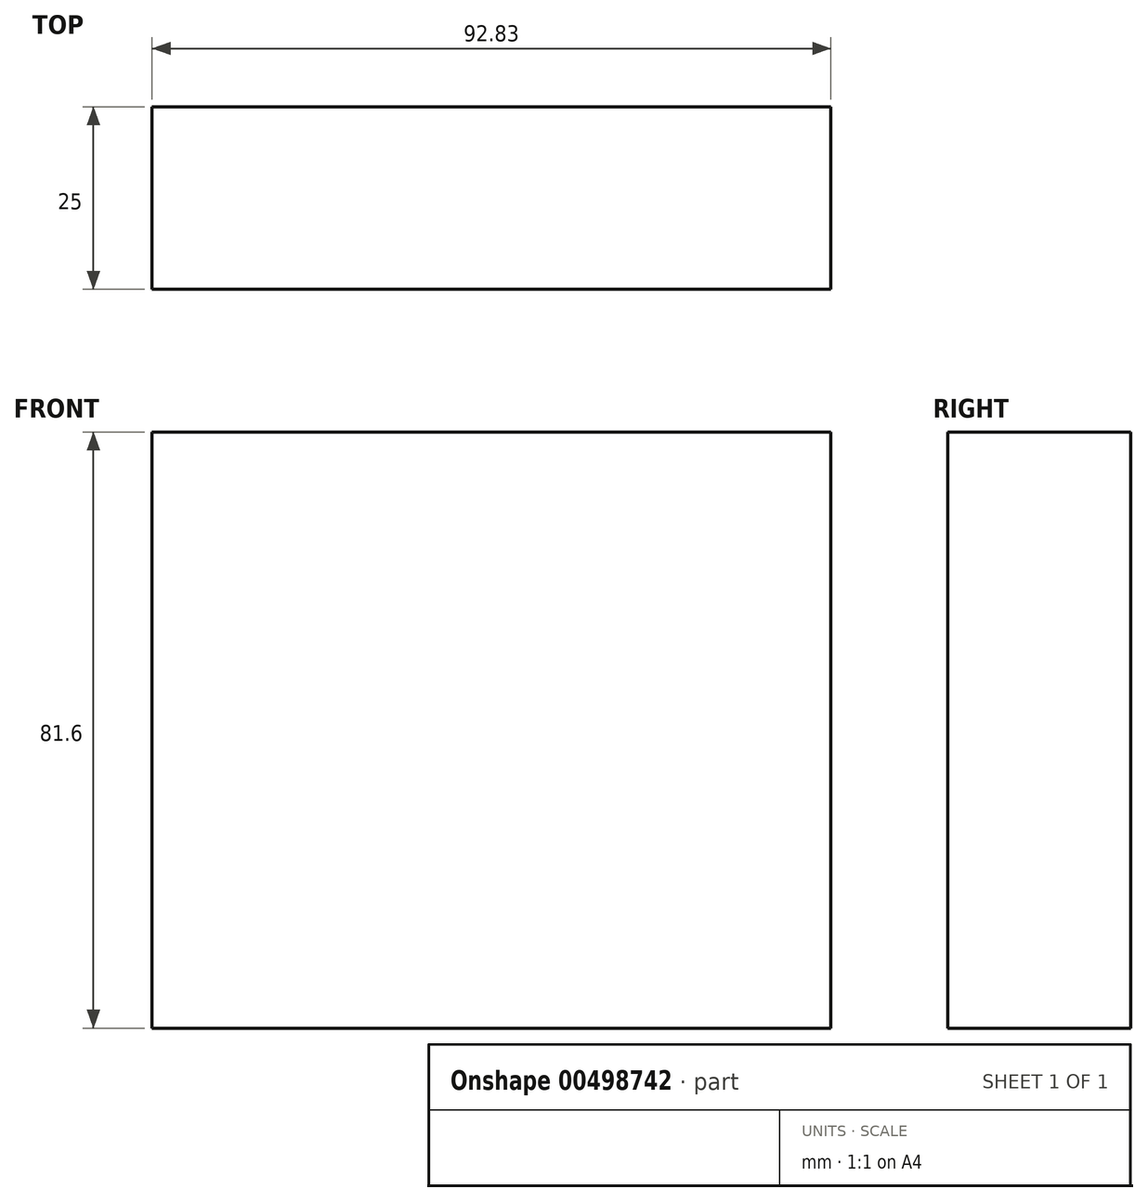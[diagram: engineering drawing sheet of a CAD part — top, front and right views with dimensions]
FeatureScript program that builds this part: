
annotation { "Feature Type Name" : "Feature", "Feature Type Description" : "" }
export const myFeature = defineFeature(function(context is Context, id is Id, definition is map)
    precondition{}
    {
        {
            var Q0;
            Q0=qCreatedBy(makeId("Front.planeOp"),FACE);
            var sketch = newSketch(context, id + "F0", { "sketchPlane" : qUnion([Q0])});
            skLineSegment(sketch, "E0.bottom", {"start": v(-170.07, 29.12) * mm, "end": v(-77.24, 29.12) * mm});
            skLineSegment(sketch, "E0.top", {"start": v(-170.07, -52.48) * mm, "end": v(-77.24, -52.48) * mm});
            skLineSegment(sketch, "E0.left", {"start": v(-170.07, 29.12) * mm, "end": v(-170.07, -52.48) * mm});
            skLineSegment(sketch, "E0.right", {"start": v(-77.24, 29.12) * mm, "end": v(-77.24, -52.48) * mm});
            skSolve(sketch);
        }
        {
            var Q0;
            Q0=makeQuery(id+"F0.imprint","IMPRINT",FACE,{"disambiguationData":[TD([[makeQuery(id+"F0.imprint","IMPRINT",EDGE,{"derivedFrom":sQuery(id+"F0.wireOp",EDGE,"E0.bottom")}),-1.0]])]});
            extrude(context, id + "F1", {"entities" : qUnion([Q0]), "depth" : 25 * mm});
        }
    });
